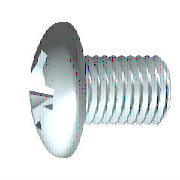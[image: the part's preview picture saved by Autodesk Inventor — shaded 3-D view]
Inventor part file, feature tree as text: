
AUTODESK INVENTOR PART (.ipt)
format: ipt  version: 2020 (Build 240168000, 168)  size: 306,176 bytes
history: native  units: mm (DEFAULTED — no unit token found)
features: extrude x2, other x1, plane x1
ambient origin geometry x7: Origin, YZ Plane, XZ Plane, X Axis, Y Axis, Z Axis, Center Point
bodies: Solid1 (feature_tree), Body (feature_tree)
feature tree (4):
  extrude  "Slot"  Depth=1.524mm
  other  "Cut"
  extrude  "Star Cut"  Depth=1.016mm
  plane  "Work Plane3"
